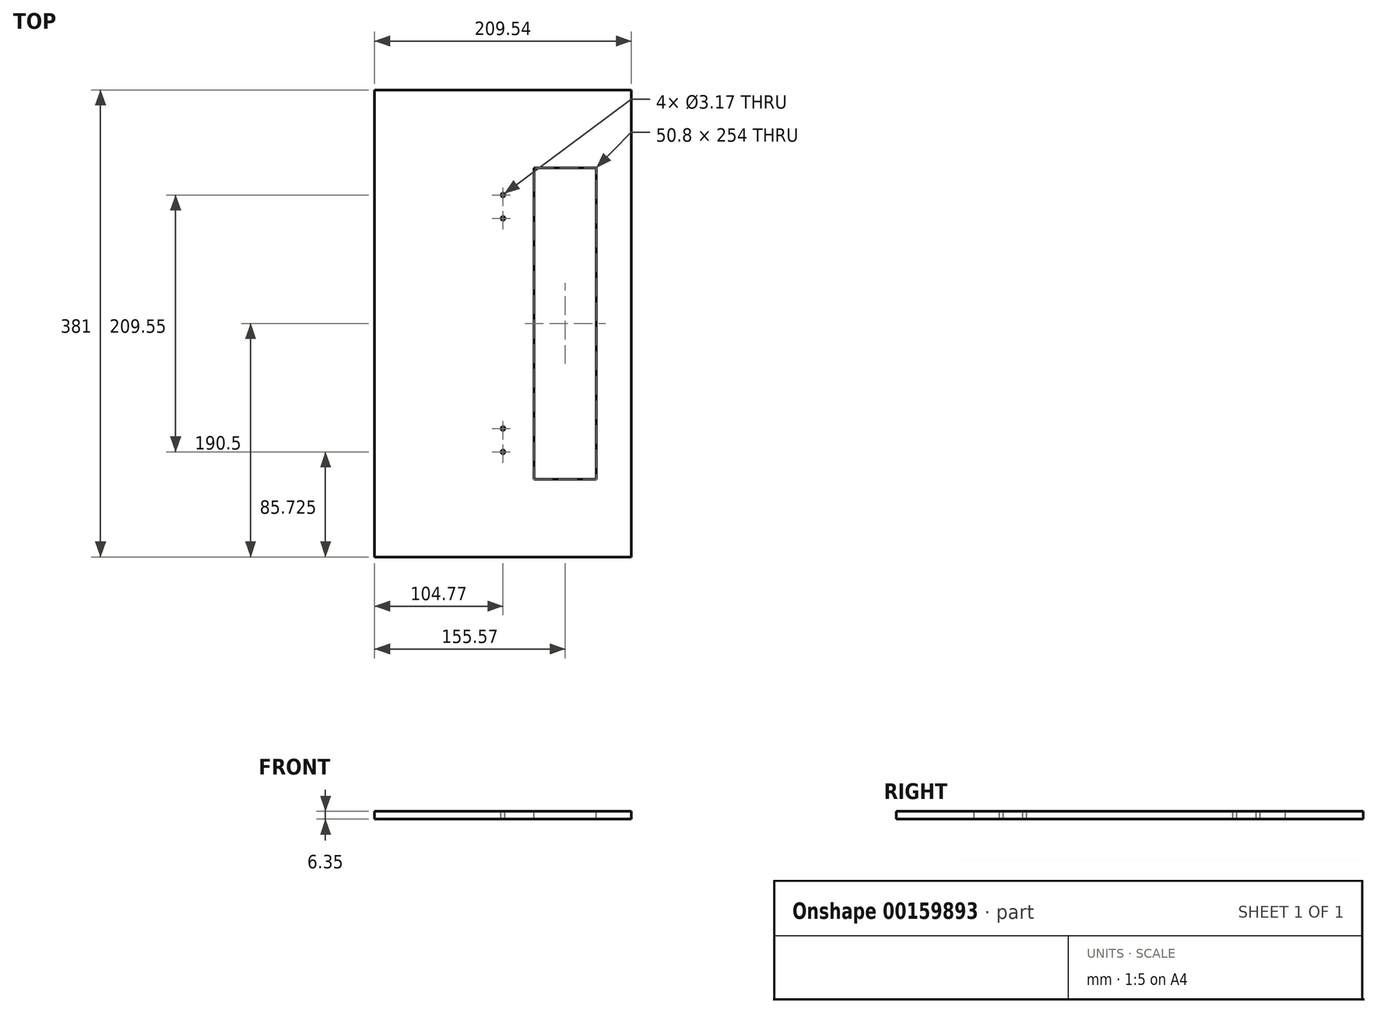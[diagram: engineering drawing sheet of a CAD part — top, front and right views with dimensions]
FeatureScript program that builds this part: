
annotation { "Feature Type Name" : "Feature", "Feature Type Description" : "" }
export const myFeature = defineFeature(function(context is Context, id is Id, definition is map)
    precondition{}
    {
        {
            var Q0;
            Q0=qCreatedBy(makeId("Top.planeOp"),FACE);
            var sketch = newSketch(context, id + "F0", { "sketchPlane" : qUnion([Q0])});
            skLineSegment(sketch, "E0.bottom", {"start": v(104.78, -190.5) * mm, "end": v(-104.78, -190.5) * mm});
            skLineSegment(sketch, "E0.top", {"start": v(104.78, 190.5) * mm, "end": v(-104.77, 190.5) * mm});
            skLineSegment(sketch, "E0.left", {"start": v(104.78, -190.5) * mm, "end": v(104.78, 190.5) * mm});
            skLineSegment(sketch, "E0.right", {"start": v(-104.78, -190.5) * mm, "end": v(-104.77, 190.5) * mm});
            skPoint(sketch, "E0.middle", {"position": v(0, 0) * mm});
            skSolve(sketch);
        }
        {
            var Q0;
            Q0=makeQuery(id+"F0.imprint","IMPRINT",FACE,{"disambiguationData":[TD([[makeQuery(id+"F0.imprint","IMPRINT",EDGE,{"derivedFrom":sQuery(id+"F0.wireOp",EDGE,"E0.bottom")}),-1.0]])]});
            extrude(context, id + "F1", {"entities" : qUnion([Q0]), "depth" : 6.35 * mm});
        }
        {
            var Q0;
            Q0=makeQuery(id+"F1.opExtrude","CAP_FACE",FACE,{"disambiguationData":[OSD([sQuery(id+"F0.wireOp",EDGE,"E0.bottom"),sQuery(id+"F0.wireOp",EDGE,"E0.top"),sQuery(id+"F0.wireOp",EDGE,"E0.left"),sQuery(id+"F0.wireOp",EDGE,"E0.right")])],"isStart":false});
            var sketch = newSketch(context, id + "F2", { "sketchPlane" : qUnion([Q0])});
            skLineSegment(sketch, "E1", {"start": v(0, -85.73) * mm, "end": v(0, 85.73) * mm, "construction": true});
            skPoint(sketch, "E2", {"position": v(0, 85.73) * mm});
            skPoint(sketch, "E3", {"position": v(0, -85.73) * mm});
            skLineSegment(sketch, "E4.bottom", {"start": v(-25.4, -127) * mm, "end": v(-76.2, -127) * mm});
            skLineSegment(sketch, "E4.top", {"start": v(-25.4, 127) * mm, "end": v(-76.2, 127) * mm});
            skLineSegment(sketch, "E4.left", {"start": v(-25.4, -127) * mm, "end": v(-25.4, 127) * mm});
            skLineSegment(sketch, "E4.right", {"start": v(-76.2, -127) * mm, "end": v(-76.2, 127) * mm});
            skPoint(sketch, "E4.middle", {"position": v(-50.8, 0) * mm});
            skPoint(sketch, "E5", {"position": v(0, 104.78) * mm});
            skPoint(sketch, "E6", {"position": v(0, -104.78) * mm});
            skLineSegment(sketch, "E7.MirrorCS", {"start": v(76.2, -127) * mm, "end": v(76.2, 127) * mm});
            skLineSegment(sketch, "E8.MirrorCS", {"start": v(25.4, -127) * mm, "end": v(25.4, 127) * mm});
            skLineSegment(sketch, "E9.MirrorCS", {"start": v(25.4, 127) * mm, "end": v(76.2, 127) * mm});
            skLineSegment(sketch, "E10.MirrorCS", {"start": v(25.4, -127) * mm, "end": v(76.2, -127) * mm});
            skPoint(sketch, "E11.MirrorP", {"position": v(50.8, 0) * mm});
            skSolve(sketch);
        }
        {
            var Q0;
            Q0=makeQuery(id+"F2.imprint","IMPRINT",FACE,{"disambiguationData":[TD([[makeQuery(id+"F2.imprint","IMPRINT",EDGE,{"derivedFrom":sQuery(id+"F2.wireOp",EDGE,"E7.MirrorCS")}),1.0]])]});
            extrude(context, id + "F3", {"entities" : qUnion([Q0]), "operationType" : NewBodyOperationType.REMOVE, "oppositeDirection" : true, "depth" : 25.4 * mm});
        }
        {
            var Q0;
            Q0=sQuery(id+"F2.wireOp",VERTEX,"E6");
            var Q1;
            Q1=sQuery(id+"F2.wireOp",VERTEX,"E3");
            var Q2;
            Q2=sQuery(id+"F2.wireOp",VERTEX,"E2");
            var Q3;
            Q3=sQuery(id+"F2.wireOp",VERTEX,"E5");
            var Q4;
            Q4=makeQuery(id+"F1.opExtrude","SWEPT_BODY",BODY,{"disambiguationData":[OSD([sQuery(id+"F0.wireOp",EDGE,"E0.bottom"),sQuery(id+"F0.wireOp",EDGE,"E0.top"),sQuery(id+"F0.wireOp",EDGE,"E0.left"),sQuery(id+"F0.wireOp",EDGE,"E0.right")])]});
            hole(context, id + "F4", {"style" : HoleStyle.SIMPLE, "endStyle" : HoleEndStyle.BLIND, "holeDiameter" : 3.17 * mm, "holeDepth" : 19.05 * mm, "locations" : qUnion([Q0, Q1, Q2, Q3]), "scope" : qUnion([Q4])});
        }
    });
